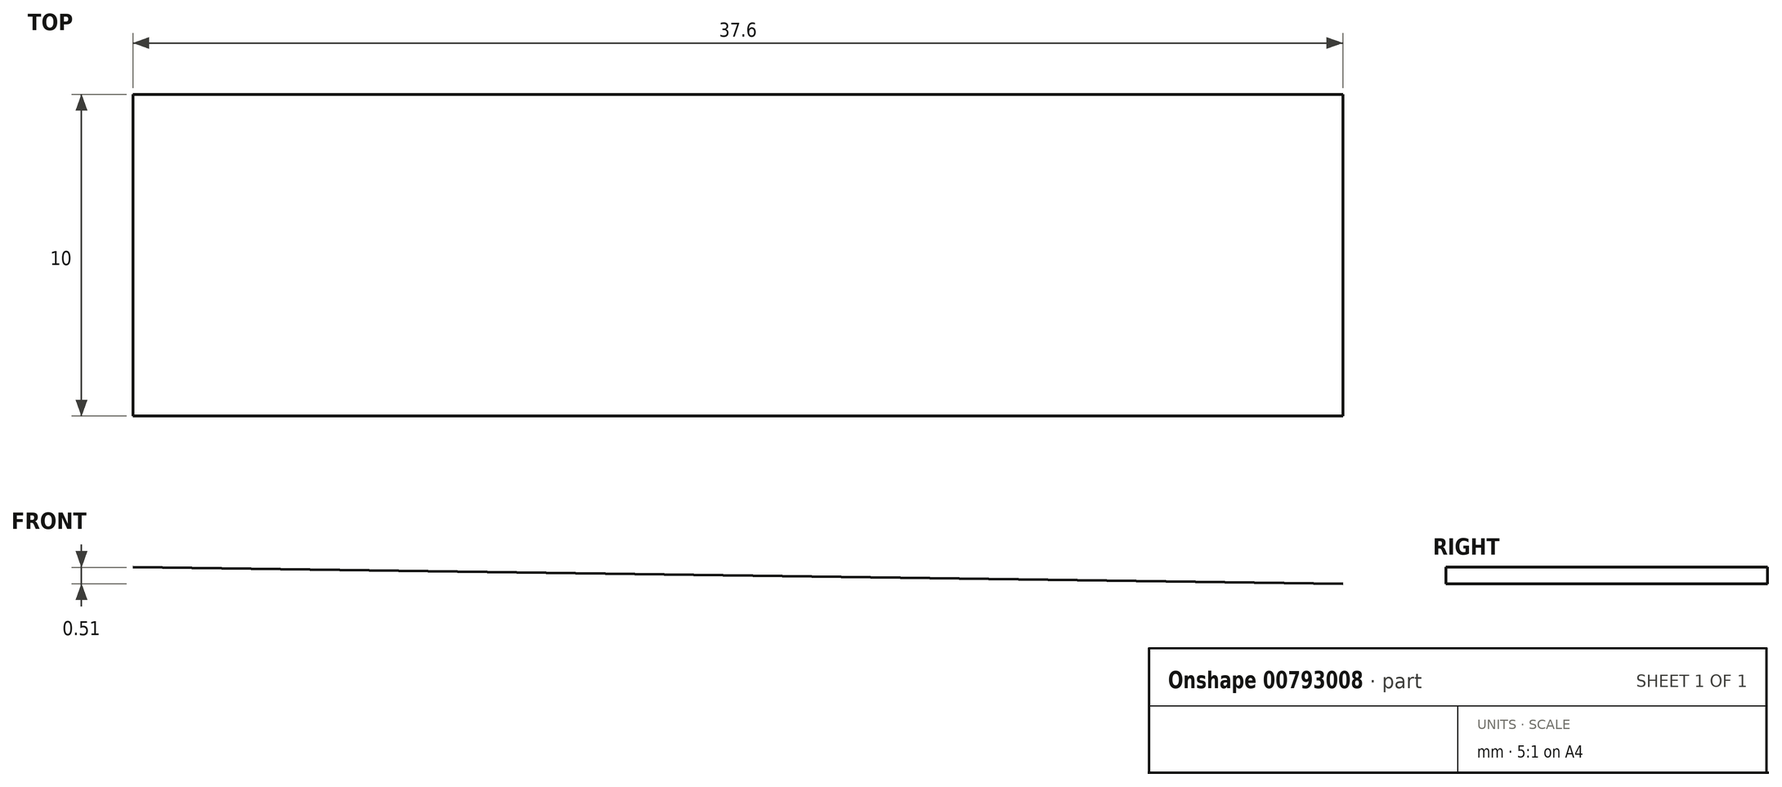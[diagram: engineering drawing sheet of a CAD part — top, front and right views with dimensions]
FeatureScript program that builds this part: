
annotation { "Feature Type Name" : "Feature", "Feature Type Description" : "" }
export const myFeature = defineFeature(function(context is Context, id is Id, definition is map)
    precondition{}
    {
        {
            var Q0;
            Q0=qCreatedBy(makeId("Front.planeOp"),FACE);
            var sketch = newSketch(context, id + "F0", { "sketchPlane" : qUnion([Q0])});
            skLineSegment(sketch, "E0", {"start": v(-17.1, 3) * mm, "end": v(-11.6, 3) * mm});
            skLineSegment(sketch, "E1", {"start": v(-11.6, 3) * mm, "end": v(-11.6, 4.58) * mm});
            skLineSegment(sketch, "E2", {"start": v(-11.6, 4.58) * mm, "end": v(-10, 4.58) * mm});
            skLineSegment(sketch, "E3", {"start": v(-10, 4.58) * mm, "end": v(-10, 3) * mm});
            skLineSegment(sketch, "E4", {"start": v(-10, 3) * mm, "end": v(-4.6, 3) * mm});
            skLineSegment(sketch, "E5", {"start": v(-4.6, 3) * mm, "end": v(-4.6, 4.58) * mm});
            skLineSegment(sketch, "E6", {"start": v(-4.6, 4.58) * mm, "end": v(-3.57, 4.58) * mm});
            skLineSegment(sketch, "E7", {"start": v(-3.57, 4.58) * mm, "end": v(-3.57, 3) * mm});
            skLineSegment(sketch, "E8", {"start": v(-3.57, 3) * mm, "end": v(-0.62, 3) * mm});
            skLineSegment(sketch, "E9", {"start": v(0, 3.63) * mm, "end": v(0, 7.52) * mm});
            skLineSegment(sketch, "E10", {"start": v(0.5, 8.02) * mm, "end": v(1.5, 8.02) * mm});
            skLineSegment(sketch, "E11", {"start": v(2, 7.52) * mm, "end": v(2, 3.63) * mm});
            skLineSegment(sketch, "E12", {"start": v(2, 0) * mm, "end": v(2, -3.84) * mm});
            skLineSegment(sketch, "E13", {"start": v(1.38, -4.47) * mm, "end": v(0.62, -4.47) * mm});
            skLineSegment(sketch, "E14", {"start": v(0, -3.84) * mm, "end": v(0, 0) * mm});
            skLineSegment(sketch, "E15", {"start": v(0, 0) * mm, "end": v(-3.57, 0) * mm});
            skLineSegment(sketch, "E16", {"start": v(-3.57, 0) * mm, "end": v(-3.57, -1.48) * mm});
            skLineSegment(sketch, "E17", {"start": v(-3.57, -1.48) * mm, "end": v(-4.6, -1.48) * mm});
            skLineSegment(sketch, "E18", {"start": v(-4.6, -1.48) * mm, "end": v(-4.6, 0) * mm});
            skLineSegment(sketch, "E19", {"start": v(-4.6, 0) * mm, "end": v(-10, 0) * mm});
            skLineSegment(sketch, "E20", {"start": v(-10, 0) * mm, "end": v(-10, -1.48) * mm});
            skLineSegment(sketch, "E21", {"start": v(-10, -1.48) * mm, "end": v(-11.6, -1.48) * mm});
            skLineSegment(sketch, "E22", {"start": v(-11.6, -1.48) * mm, "end": v(-11.6, 0) * mm});
            skLineSegment(sketch, "E23", {"start": v(-11.6, 0) * mm, "end": v(-17.1, 0) * mm});
            skLineSegment(sketch, "E24", {"start": v(-17.6, 2.5) * mm, "end": v(-17.6, 0.5) * mm});
            skPoint(sketch, "E25.visualSharp", {"position": v(-17.6, 0) * mm});
            skArc(sketch, "E25.filletArc", {"start": v(-17.6, 0.5) * mm, "mid": v(-17.45, 0.15) * mm, "end": v(-17.1, 0) * mm});
            skPoint(sketch, "E26.visualSharp", {"position": v(-17.6, 3) * mm});
            skArc(sketch, "E26.filletArc", {"start": v(-17.1, 3) * mm, "mid": v(-17.45, 2.86) * mm, "end": v(-17.6, 2.5) * mm});
            skLineSegment(sketch, "E27", {"start": v(20, 3) * mm, "end": v(20, 0) * mm});
            skLineSegment(sketch, "E28", {"start": v(2.62, 3) * mm, "end": v(10, 3) * mm});
            skLineSegment(sketch, "E29", {"start": v(10, 3) * mm, "end": v(10, 6.68) * mm});
            skLineSegment(sketch, "E30", {"start": v(10, 6.68) * mm, "end": v(12, 6.68) * mm});
            skLineSegment(sketch, "E31", {"start": v(12, 6.68) * mm, "end": v(12, 3) * mm});
            skLineSegment(sketch, "E32", {"start": v(12, 3) * mm, "end": v(20, 3) * mm});
            skLineSegment(sketch, "E33", {"start": v(2, 0) * mm, "end": v(9.41, 0) * mm});
            skLineSegment(sketch, "E34", {"start": v(10.03, -0.62) * mm, "end": v(10.03, -2.64) * mm});
            skLineSegment(sketch, "E35", {"start": v(10.03, -2.64) * mm, "end": v(12.03, -2.64) * mm});
            skLineSegment(sketch, "E36", {"start": v(12.03, -2.64) * mm, "end": v(12.03, -0.62) * mm});
            skLineSegment(sketch, "E37", {"start": v(12.66, 0) * mm, "end": v(20, 0) * mm});
            skPoint(sketch, "E38.visualSharp", {"position": v(12.03, 0) * mm});
            skArc(sketch, "E38.filletArc", {"start": v(12.66, 0) * mm, "mid": v(12.22, -0.18) * mm, "end": v(12.03, -0.62) * mm});
            skPoint(sketch, "E39.visualSharp", {"position": v(0, 8.02) * mm});
            skArc(sketch, "E39.filletArc", {"start": v(0.5, 8.02) * mm, "mid": v(0.15, 7.87) * mm, "end": v(0, 7.52) * mm});
            skPoint(sketch, "E40.visualSharp", {"position": v(2, 8.02) * mm});
            skArc(sketch, "E40.filletArc", {"start": v(2, 7.52) * mm, "mid": v(1.85, 7.87) * mm, "end": v(1.5, 8.02) * mm});
            skPoint(sketch, "E41.visualSharp", {"position": v(0, 3) * mm});
            skArc(sketch, "E41.filletArc", {"start": v(-0.62, 3) * mm, "mid": v(-0.18, 3.18) * mm, "end": v(0, 3.63) * mm});
            skPoint(sketch, "E42.visualSharp", {"position": v(2, 3) * mm});
            skArc(sketch, "E42.filletArc", {"start": v(2, 3.63) * mm, "mid": v(2.18, 3.18) * mm, "end": v(2.62, 3) * mm});
            skPoint(sketch, "E43.visualSharp", {"position": v(10.03, 0) * mm});
            skArc(sketch, "E43.filletArc", {"start": v(10.03, -0.62) * mm, "mid": v(9.85, -0.18) * mm, "end": v(9.41, 0) * mm});
            skPoint(sketch, "E44.visualSharp", {"position": v(0, -4.47) * mm});
            skArc(sketch, "E44.filletArc", {"start": v(0, -3.84) * mm, "mid": v(0.18, -4.28) * mm, "end": v(0.62, -4.47) * mm});
            skPoint(sketch, "E45.visualSharp", {"position": v(2, -4.47) * mm});
            skArc(sketch, "E45.filletArc", {"start": v(1.38, -4.47) * mm, "mid": v(1.82, -4.28) * mm, "end": v(2, -3.84) * mm});
            skLineSegment(sketch, "E46", {"start": v(-17.6, 2.13) * mm, "end": v(20, 2.93) * mm});
            skLineSegment(sketch, "E47", {"start": v(-17.6, 1.01) * mm, "end": v(20, 0.5) * mm});
            skSolve(sketch);
        }
        {
            var Q0;
            {var subQ0=sQuery(id+"F0.wireOp",EDGE,"E46");Q0=makeQuery(id+"F0.imprint","IMPRINT",FACE,{"disambiguationData":[TD([[makeQuery(id+"F0.imprint","IMPRINT",EDGE,{"derivedFrom":subQ0}),-1.0]])]});}
            var Q1;
            Q1=makeQuery(id+"F0.imprint","IMPRINT",FACE,{"disambiguationData":[TD([[makeQuery(id+"F0.imprint","IMPRINT",EDGE,{"derivedFrom":sQuery(id+"F0.wireOp",EDGE,"E0")}),-1.0]])]});
            var Q2;
            Q2=makeQuery(id+"F0.imprint","IMPRINT",FACE,{"disambiguationData":[TD([[makeQuery(id+"F0.imprint","IMPRINT",EDGE,{"derivedFrom":sQuery(id+"F0.wireOp",EDGE,"E12")}),-1.0]])]});
            var Q3;
            Q3=sQuery(id+"F0.wireOp",EDGE,"E47");
            extrude(context, id + "F1", {"entities" : qUnion([Q0, Q1, Q2]), "bodyType" : ToolBodyType.SURFACE, "surfaceEntities" : qUnion([Q3]), "depth" : 10 * mm, "offsetDistance" : 25 * mm});
        }
    });
